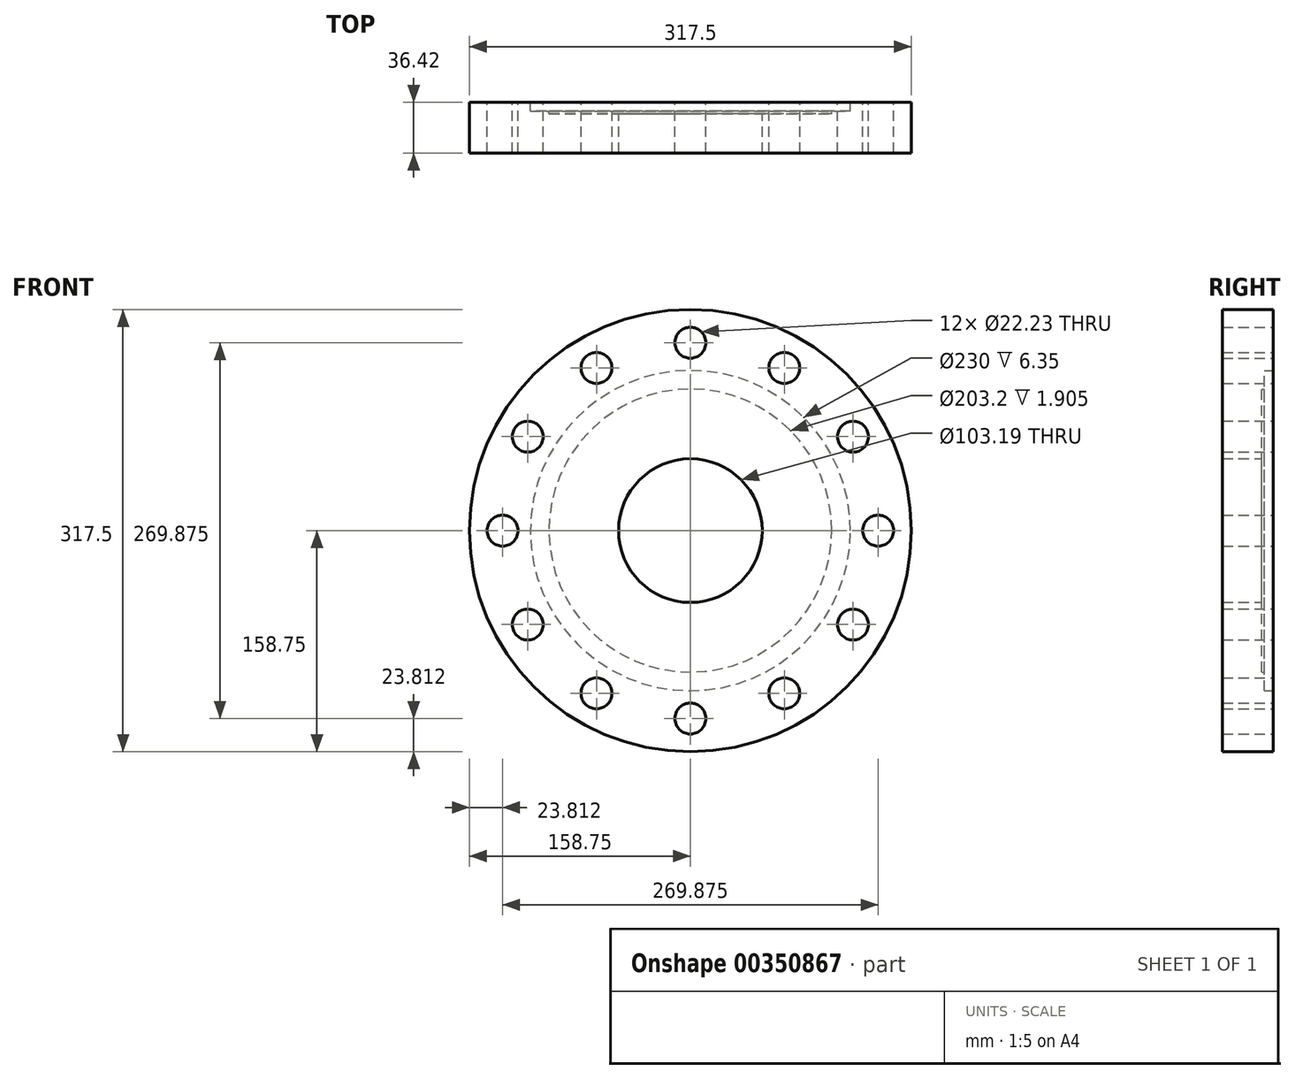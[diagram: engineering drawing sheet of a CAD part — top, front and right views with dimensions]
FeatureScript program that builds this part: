
annotation { "Feature Type Name" : "Feature", "Feature Type Description" : "" }
export const myFeature = defineFeature(function(context is Context, id is Id, definition is map)
    precondition{}
    {
        {
            var Q0;
            Q0=qCreatedBy(makeId("Front.planeOp"),FACE);
            var sketch = newSketch(context, id + "F0", { "sketchPlane" : qUnion([Q0])});
            skCircle(sketch, "E0", {"center": v(0, 0) * mm, "radius": 158.75 * mm});
            skCircle(sketch, "E1", {"center": v(0, 0) * mm, "radius": 134.94 * mm, "construction": true});
            skCircle(sketch, "E2", {"center": v(0, 134.94) * mm, "radius": 11.11 * mm});
            skCircle(sketch, "E3.1.0", {"center": v(-67.47, 116.86) * mm, "radius": 11.11 * mm});
            skCircle(sketch, "E3.2.0", {"center": v(-116.86, 67.47) * mm, "radius": 11.11 * mm});
            skCircle(sketch, "E4.1.3.0", {"center": v(-134.94, 0) * mm, "radius": 11.11 * mm});
            skCircle(sketch, "E4.1.4.0", {"center": v(-116.86, -67.47) * mm, "radius": 11.11 * mm});
            skCircle(sketch, "E4.1.5.0", {"center": v(-67.47, -116.86) * mm, "radius": 11.11 * mm});
            skCircle(sketch, "E4.1.6.0", {"center": v(0, -134.94) * mm, "radius": 11.11 * mm});
            skCircle(sketch, "E4.1.7.0", {"center": v(67.47, -116.86) * mm, "radius": 11.11 * mm});
            skCircle(sketch, "E4.1.8.0", {"center": v(116.86, -67.47) * mm, "radius": 11.11 * mm});
            skCircle(sketch, "E4.1.9.0", {"center": v(134.94, 0) * mm, "radius": 11.11 * mm});
            skCircle(sketch, "E4.1.10.0", {"center": v(116.86, 67.47) * mm, "radius": 11.11 * mm});
            skCircle(sketch, "E4.1.11.0", {"center": v(67.47, 116.86) * mm, "radius": 11.11 * mm});
            skSolve(sketch);
        }
        {
            var Q0;
            Q0=makeQuery(id+"F0.imprint","IMPRINT",FACE,{"disambiguationData":[TD([[makeQuery(id+"F0.imprint","IMPRINT",EDGE,{"derivedFrom":sQuery(id+"F0.wireOp",EDGE,"E0")}),1.0]])]});
            var Q1;
            Q1=sQuery(id+"F0.wireOp",EDGE,"E0");
            extrude(context, id + "F1", {"entities" : qUnion([Q0]), "surfaceEntities" : qUnion([Q1]), "depth" : 36.42 * mm});
        }
        {
            var Q0;
            Q0=makeQuery(id+"F0.imprint","IMPRINT",FACE,{"disambiguationData":[TD([[makeQuery(id+"F0.imprint","IMPRINT",EDGE,{"derivedFrom":sQuery(id+"F0.wireOp",EDGE,"E0")}),1.0]])]});
            var sketch = newSketch(context, id + "F2", { "sketchPlane" : qUnion([Q0])});
            skCircle(sketch, "E5", {"center": v(0, 0) * mm, "radius": 115 * mm});
            skCircle(sketch, "E6", {"center": v(0, 0) * mm, "radius": 101.6 * mm});
            skCircle(sketch, "E7", {"center": v(0, 0) * mm, "radius": 51.6 * mm});
            skSolve(sketch);
        }
        {
            var Q0;
            Q0=makeQuery(id+"F2.imprint","IMPRINT",FACE,{"disambiguationData":[TD([[makeQuery(id+"F2.imprint","IMPRINT",EDGE,{"derivedFrom":sQuery(id+"F2.wireOp",EDGE,"E5")}),1.0]])]});
            extrude(context, id + "F3", {"entities" : qUnion([Q0]), "operationType" : NewBodyOperationType.REMOVE, "depth" : 6.35 * mm});
        }
        {
            var Q0;
            Q0=makeQuery(id+"F2.imprint","IMPRINT",FACE,{"disambiguationData":[TD([[makeQuery(id+"F2.imprint","IMPRINT",EDGE,{"derivedFrom":sQuery(id+"F2.wireOp",EDGE,"E6")}),1.0]])]});
            extrude(context, id + "F4", {"entities" : qUnion([Q0]), "operationType" : NewBodyOperationType.REMOVE, "depth" : 8.25 * mm});
        }
        {
            var Q0;
            Q0=makeQuery(id+"F2.imprint","IMPRINT",FACE,{"disambiguationData":[TD([[makeQuery(id+"F2.imprint","IMPRINT",EDGE,{"derivedFrom":sQuery(id+"F2.wireOp",EDGE,"E7")}),1.0]])]});
            extrude(context, id + "F5", {"entities" : qUnion([Q0]), "operationType" : NewBodyOperationType.REMOVE, "depth" : 36.42 * mm});
        }
    });
